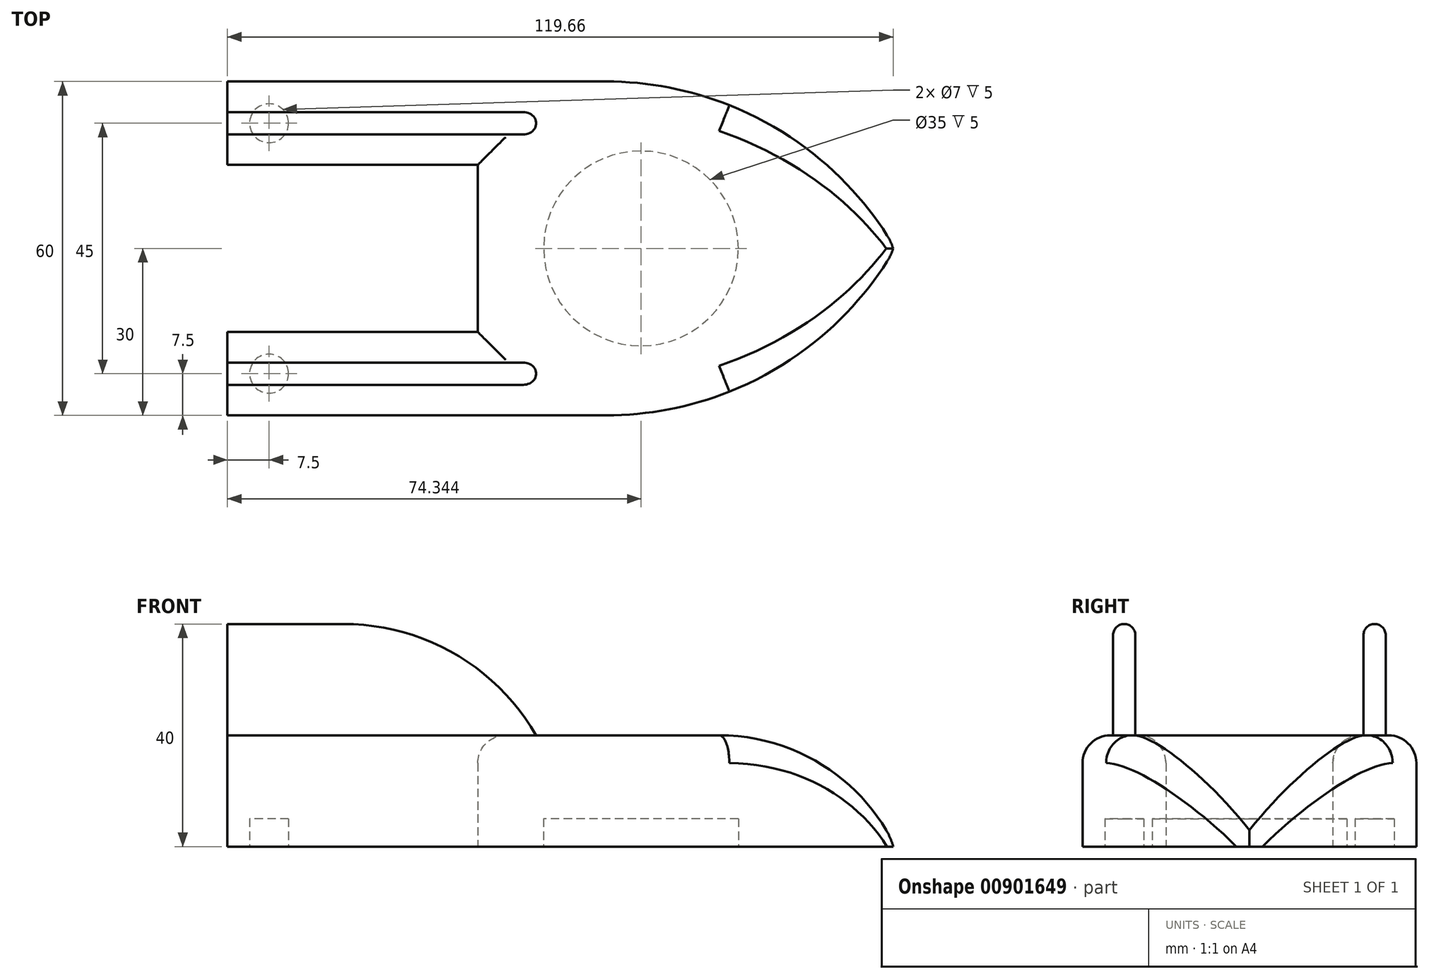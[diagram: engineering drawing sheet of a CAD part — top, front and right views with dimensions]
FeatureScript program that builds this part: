
annotation { "Feature Type Name" : "Feature", "Feature Type Description" : "" }
export const myFeature = defineFeature(function(context is Context, id is Id, definition is map)
    precondition{}
    {
        {
            assignVariable(context, id + "F0", {"name" : "width", "anyValue" : 20 * mm});
        }
        {
            var Q0;
            Q0=qCreatedBy(makeId("Top.planeOp"),FACE);
            var sketch = newSketch(context, id + "F1", { "sketchPlane" : qUnion([Q0])});
            skLineSegment(sketch, "E0.bottom", {"start": v(23.04, -30) * mm, "end": v(-45, -30) * mm});
            skLineSegment(sketch, "E0.top", {"start": v(23.04, 30) * mm, "end": v(-45, 30) * mm});
            skLineSegment(sketch, "E0.right", {"start": v(-45, -30) * mm, "end": v(-45, -15) * mm});
            skCircle(sketch, "E1", {"center": v(29.34, 0) * mm, "radius": 17.5 * mm});
            skLineSegment(sketch, "E2.bottom", {"start": v(0, 15) * mm, "end": v(-45, 15) * mm});
            skLineSegment(sketch, "E2.top", {"start": v(0, -15) * mm, "end": v(-45, -15) * mm});
            skLineSegment(sketch, "E2.left", {"start": v(0, 15) * mm, "end": v(0, -15) * mm});
            skLineSegment(sketch, "E3.trimOffspring", {"start": v(-45, 15) * mm, "end": v(-45, 30) * mm});
            skArc(sketch, "E4", {"start": v(75, 0) * mm, "mid": v(53.04, 21.96) * mm, "end": v(23.04, 30) * mm});
            skArc(sketch, "E5", {"start": v(23.04, -30) * mm, "mid": v(53.04, -21.96) * mm, "end": v(75, 0) * mm});
            skCircle(sketch, "E6", {"center": v(29.34, 0) * mm, "radius": 29.34 * mm, "construction": true});
            skCircle(sketch, "E7", {"center": v(-37.5, 22.5) * mm, "radius": 3.5 * mm});
            skCircle(sketch, "E8", {"center": v(-37.5, 22.5) * mm, "radius": 7.5 * mm, "construction": true});
            skCircle(sketch, "E9.MirrorC", {"center": v(-37.5, -22.5) * mm, "radius": 3.5 * mm});
            skSolve(sketch);
        }
        {
            var Q0;
            Q0 = qSketchRegion(id + "F1", true);
            var Q1;
            Q1=makeQuery(id+"F1.imprint","IMPRINT",FACE,{"disambiguationData":[TD([[makeQuery(id+"F1.imprint","IMPRINT",EDGE,{"derivedFrom":sQuery(id+"F1.wireOp",EDGE,"E1")}),1.0]])]});
            var Q2;
            Q2=makeQuery(id+"F1.imprint","IMPRINT",FACE,{"disambiguationData":[TD([[makeQuery(id+"F1.imprint","IMPRINT",EDGE,{"derivedFrom":sQuery(id+"F1.wireOp",EDGE,"E7")}),-1.0]])]});
            var Q3;
            Q3=makeQuery(id+"F1.imprint","IMPRINT",FACE,{"disambiguationData":[TD([[makeQuery(id+"F1.imprint","IMPRINT",EDGE,{"derivedFrom":sQuery(id+"F1.wireOp",EDGE,"E9.MirrorC")}),1.0]])]});
            var Q4;
            Q4=makeQuery(id+"F1.imprint","IMPRINT",FACE,{"disambiguationData":[TD([[makeQuery(id+"F1.imprint","IMPRINT",EDGE,{"derivedFrom":sQuery(id+"F1.wireOp",EDGE,"E7")}),1.0]])]});
            extrude(context, id + "F2", {"entities" : qUnion([Q0, Q1, Q2, Q3, Q4]), "depth" : getVariable(context, 'width'), "offsetDistance" : 25 * mm});
        }
        {
            var Q0;
            Q0=makeQuery(id+"F2.opExtrude","SWEPT_FACE",FACE,{"disambiguationData":[OSD([sQuery(id+"F1.wireOp",EDGE,"E0.top")])]});
            var sketch = newSketch(context, id + "F3", { "sketchPlane" : qUnion([Q0])});
            skPoint(sketch, "E10", {"position": v(0, 5) * mm});
            skSolve(sketch);
        }
        {
            var Q0;
            Q0=makeQuery(id+"F1.imprint","IMPRINT",FACE,{"disambiguationData":[TD([[makeQuery(id+"F1.imprint","IMPRINT",EDGE,{"derivedFrom":sQuery(id+"F1.wireOp",EDGE,"E1")}),1.0]])]});
            var Q1;
            Q1=makeQuery(id+"F1.imprint","IMPRINT",FACE,{"disambiguationData":[TD([[makeQuery(id+"F1.imprint","IMPRINT",EDGE,{"derivedFrom":sQuery(id+"F1.wireOp",EDGE,"E9.MirrorC")}),1.0]])]});
            var Q2;
            Q2=makeQuery(id+"F1.imprint","IMPRINT",FACE,{"disambiguationData":[TD([[makeQuery(id+"F1.imprint","IMPRINT",EDGE,{"derivedFrom":sQuery(id+"F1.wireOp",EDGE,"E7")}),1.0]])]});
            var Q3;
            Q3=sQuery(id+"F3.wireOp",VERTEX,"E10");
            extrude(context, id + "F4", {"entities" : qUnion([Q0, Q1, Q2]), "operationType" : NewBodyOperationType.REMOVE, "endBound" : BoundingType.UP_TO_VERTEX, "depth" : getVariable(context, 'width') - 10 * mm, "endBoundEntityVertex" : qUnion([Q3]), "offsetDistance" : 25 * mm});
        }
        {
            var Q0;
            Q0=qCreatedBy(makeId("Front.planeOp"),FACE);
            var sketch = newSketch(context, id + "F5", { "sketchPlane" : qUnion([Q0])});
            skPoint(sketch, "E11.0", {"position": v(75, 0) * mm});
            skLineSegment(sketch, "E12.0", {"start": v(75, 20) * mm, "end": v(23.04, 20) * mm});
            skArc(sketch, "E13", {"start": v(75, 0) * mm, "mid": v(62.09, 14.58) * mm, "end": v(43.38, 20) * mm});
            skLineSegment(sketch, "E14", {"start": v(75, 0) * mm, "end": v(75, 20) * mm});
            skSolve(sketch);
        }
        {
            var Q0;
            Q0 = qSketchRegion(id + "F5", true);
            extrude(context, id + "F6", {"entities" : qUnion([Q0]), "operationType" : NewBodyOperationType.REMOVE, "endBound" : BoundingType.THROUGH_ALL, "oppositeDirection" : true, "depth" : 100 * mm, "offsetDistance" : 25 * mm, "hasSecondDirection" : true, "secondDirectionBound" : SecondDirectionBoundingType.THROUGH_ALL, "secondDirectionOppositeDirection" : false, "secondDirectionDepth" : 25 * mm});
        }
        {
            var Q0;
            Q0=makeQuery(id+"F2.opExtrude","CAP_FACE",FACE,{"disambiguationData":[OSD([sQuery(id+"F1.wireOp",EDGE,"E0.bottom"),sQuery(id+"F1.wireOp",EDGE,"E0.top"),sQuery(id+"F1.wireOp",EDGE,"E0.right"),sQuery(id+"F1.wireOp",EDGE,"E2.bottom"),sQuery(id+"F1.wireOp",EDGE,"E2.top"),sQuery(id+"F1.wireOp",EDGE,"E2.left"),sQuery(id+"F1.wireOp",EDGE,"E3.trimOffspring"),sQuery(id+"F1.wireOp",EDGE,"E4"),sQuery(id+"F1.wireOp",EDGE,"E5")])],"isStart":false});
            var sketch = newSketch(context, id + "F7", { "sketchPlane" : qUnion([Q0])});
            skLineSegment(sketch, "E15.0", {"start": v(-45, 15) * mm, "end": v(-45, 30) * mm, "construction": true});
            skLineSegment(sketch, "E16", {"start": v(-45, 22.5) * mm, "end": v(10.5, 22.5) * mm, "construction": true});
            skCircle(sketch, "E17.0", {"center": v(29.34, 0) * mm, "radius": 29.34 * mm, "construction": true});
            skPoint(sketch, "E18", {"position": v(-17.25, 22.5) * mm});
            skLineSegment(sketch, "E19.bottom", {"start": v(-45, 20.5) * mm, "end": v(10.5, 20.5) * mm});
            skLineSegment(sketch, "E19.top", {"start": v(-45, 24.5) * mm, "end": v(10.5, 24.5) * mm});
            skLineSegment(sketch, "E19.left", {"start": v(-45, 20.5) * mm, "end": v(-45, 24.5) * mm});
            skLineSegment(sketch, "E19.right", {"start": v(10.5, 20.5) * mm, "end": v(10.5, 24.5) * mm});
            skSolve(sketch);
        }
        {
            var Q0;
            Q0=makeQuery(id+"F7.imprint","IMPRINT",FACE,{"disambiguationData":[TD([[makeQuery(id+"F7.imprint","IMPRINT",EDGE,{"derivedFrom":sQuery(id+"F7.wireOp",EDGE,"E19.bottom")}),1.0]])]});
            extrude(context, id + "F8", {"entities" : qUnion([Q0]), "operationType" : NewBodyOperationType.ADD, "depth" : getVariable(context, 'width'), "offsetDistance" : 25 * mm});
        }
        {
            var Q0;
            Q0=makeQuery(id+"F11.opPattern","COPY",EDGE,{"derivedFrom":makeQuery(id+"F8.opExtrude","CAP_EDGE",EDGE,{"disambiguationData":[OSD([sQuery(id+"F7.wireOp",EDGE,"E19.right")])],"isStart":false}),"instanceName":"1"});
            var Q1;
            Q1=makeQuery(id+"F8.opExtrude","CAP_EDGE",EDGE,{"disambiguationData":[OSD([sQuery(id+"F7.wireOp",EDGE,"E19.right")])],"isStart":false});
            fillet(context, id + "F9", {"entities" : qUnion([Q0, Q1]), "radius" : 40 * mm, "tangentPropagation" : true, "allowEdgeOverflow" : false});
        }
        {
            var Q0;
            Q0=makeQuery(id+"F8.opExtrude","CAP_EDGE",EDGE,{"disambiguationData":[OSD([sQuery(id+"F7.wireOp",EDGE,"E19.bottom")])],"isStart":true});
            var Q1;
            Q1=makeQuery(id+"F8.opExtrude","CAP_EDGE",EDGE,{"disambiguationData":[OSD([sQuery(id+"F7.wireOp",EDGE,"E19.top")])],"isStart":true});
            var Q2;
            Q2=makeQuery(id+"F9.opFillet","BLEND_EDGE",EDGE,{"blendedFrom":[makeQuery(id+"F8.opExtrude","CAP_EDGE",EDGE,{"disambiguationData":[OSD([sQuery(id+"F7.wireOp",EDGE,"E19.right")])],"isStart":false}),makeQuery(id+"F8.opExtrude","SWEPT_FACE",FACE,{"disambiguationData":[OSD([sQuery(id+"F7.wireOp",EDGE,"E19.bottom")])]})],"blendedInto":[makeQuery(id+"F8.opExtrude","SWEPT_FACE",FACE,{"disambiguationData":[OSD([sQuery(id+"F7.wireOp",EDGE,"E19.bottom")])]})]});
            var Q3;
            Q3=makeQuery(id+"F9.opFillet","BLEND_EDGE",EDGE,{"blendedFrom":[makeQuery(id+"F8.opExtrude","CAP_EDGE",EDGE,{"disambiguationData":[OSD([sQuery(id+"F7.wireOp",EDGE,"E19.right")])],"isStart":false}),makeQuery(id+"F8.opExtrude","SWEPT_FACE",FACE,{"disambiguationData":[OSD([sQuery(id+"F7.wireOp",EDGE,"E19.top")])]})],"blendedInto":[makeQuery(id+"F8.opExtrude","SWEPT_FACE",FACE,{"disambiguationData":[OSD([sQuery(id+"F7.wireOp",EDGE,"E19.top")])]})]});
            fillet(context, id + "F10", {"entities" : qUnion([Q0, Q1, Q2, Q3]), "radius" : 2 * mm, "tangentPropagation" : true, "allowEdgeOverflow" : false});
        }
        {
            var Q0;
            Q0=makeQuery(id+"F2.opExtrude","SWEPT_BODY",BODY,{"disambiguationData":[OSD([sQuery(id+"F1.wireOp",EDGE,"E0.bottom"),sQuery(id+"F1.wireOp",EDGE,"E0.top"),sQuery(id+"F1.wireOp",EDGE,"E0.right"),sQuery(id+"F1.wireOp",EDGE,"E2.bottom"),sQuery(id+"F1.wireOp",EDGE,"E2.top"),sQuery(id+"F1.wireOp",EDGE,"E2.left"),sQuery(id+"F1.wireOp",EDGE,"E3.trimOffspring"),sQuery(id+"F1.wireOp",EDGE,"E4"),sQuery(id+"F1.wireOp",EDGE,"E5")])]});
            var Q1;
            Q1=qCreatedBy(makeId("Front.planeOp"),FACE);
            mirror(context, id + "F11", {"operationType" : NewBodyOperationType.ADD, "entities" : qUnion([Q0]), "mirrorPlane" : qUnion([Q1])});
        }
        {
            var Q0;
            Q0=makeQuery(id+"F2.opExtrude","CAP_EDGE",EDGE,{"disambiguationData":[OSD([sQuery(id+"F1.wireOp",EDGE,"E0.bottom")])],"isStart":false});
            var Q1;
            Q1=makeQuery(id+"F2.opExtrude","CAP_EDGE",EDGE,{"disambiguationData":[OSD([sQuery(id+"F1.wireOp",EDGE,"E0.top")])],"isStart":false});
            var Q2;
            Q2=makeQuery(id+"F2.opExtrude","CAP_EDGE",EDGE,{"disambiguationData":[OSD([sQuery(id+"F1.wireOp",EDGE,"E2.bottom")])],"isStart":false});
            var Q3;
            Q3=makeQuery(id+"F2.opExtrude","CAP_EDGE",EDGE,{"disambiguationData":[OSD([sQuery(id+"F1.wireOp",EDGE,"E2.top")])],"isStart":false});
            fillet(context, id + "F12", {"entities" : qUnion([Q0, Q1, Q2, Q3]), "radius" : 5 * mm, "tangentPropagation" : true, "allowEdgeOverflow" : false});
        }
        {
            var Q0;
            Q0=makeQuery(id+"F2.opExtrude","CAP_EDGE",EDGE,{"disambiguationData":[OSD([sQuery(id+"F1.wireOp",EDGE,"E2.left")])],"isStart":false});
            fillet(context, id + "F13", {"entities" : qUnion([Q0]), "radius" : 5 * mm, "tangentPropagation" : true, "allowEdgeOverflow" : false});
        }
    });
